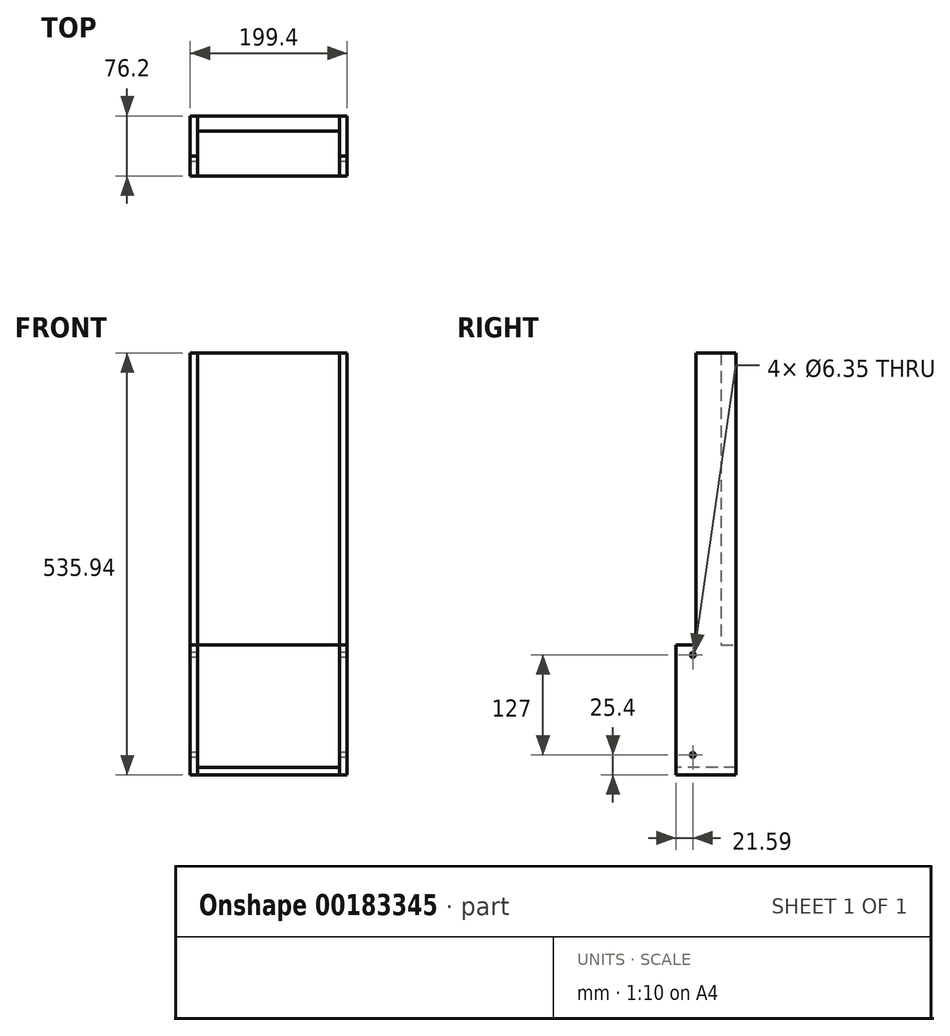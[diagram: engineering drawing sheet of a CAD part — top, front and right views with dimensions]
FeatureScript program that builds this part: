
annotation { "Feature Type Name" : "Feature", "Feature Type Description" : "" }
export const myFeature = defineFeature(function(context is Context, id is Id, definition is map)
    precondition{}
    {
        {
            var Q0;
            Q0=qCreatedBy(makeId("Front.planeOp"),FACE);
            var sketch = newSketch(context, id + "F0", { "sketchPlane" : qUnion([Q0])});
            skLineSegment(sketch, "E0.bottom", {"start": v(90.17, 185.42) * mm, "end": v(-90.17, 185.42) * mm});
            skLineSegment(sketch, "E0.top", {"start": v(90.17, -185.42) * mm, "end": v(-90.17, -185.42) * mm});
            skLineSegment(sketch, "E0.left", {"start": v(90.17, 185.42) * mm, "end": v(90.17, -185.42) * mm});
            skLineSegment(sketch, "E0.right", {"start": v(-90.17, 185.42) * mm, "end": v(-90.17, -185.42) * mm});
            skPoint(sketch, "E0.middle", {"position": v(0, 0) * mm});
            skSolve(sketch);
        }
        {
            var Q0;
            Q0 = qSketchRegion(id + "F0", true);
            extrude(context, id + "F1", {"entities" : qUnion([Q0]), "depth" : 19.05 * mm});
        }
        {
            var Q0;
            Q0=qCreatedBy(makeId("Right.planeOp"),FACE);
            var sketch = newSketch(context, id + "F2", { "sketchPlane" : qUnion([Q0])});
            skLineSegment(sketch, "E1", {"start": v(0, 0) * mm, "end": v(-162.56, 0) * mm, "construction": true});
            skLineSegment(sketch, "E2", {"start": v(-162.56, 0) * mm, "end": v(-162.56, -490.22) * mm, "construction": true});
            skLineSegment(sketch, "E3", {"start": v(0, 0) * mm, "end": v(0, -490.22) * mm, "construction": true});
            skLineSegment(sketch, "E4", {"start": v(468.47, -490.22) * mm, "end": v(-664.71, -490.22) * mm, "construction": true});
            skLineSegment(sketch, "E5", {"start": v(0, -325.12) * mm, "end": v(-162.56, -325.12) * mm, "construction": true});
            skLineSegment(sketch, "E6", {"start": v(-54.6, -325.12) * mm, "end": v(-54.6, -198.12) * mm, "construction": true});
            skLineSegment(sketch, "E7", {"start": v(-54.6, -198.12) * mm, "end": v(-162.56, -198.12) * mm, "construction": true});
            skSolve(sketch);
        }
        {
            var Q0;
            Q0=makeQuery(id+"F1.opExtrude","SWEPT_FACE",FACE,{"disambiguationData":[OSD([sQuery(id+"F0.wireOp",EDGE,"E0.right")])]});
            var sketch = newSketch(context, id + "F3", { "sketchPlane" : qUnion([Q0])});
            skLineSegment(sketch, "E8.bottom", {"start": v(0, 185.42) * mm, "end": v(50.8, 185.42) * mm});
            skLineSegment(sketch, "E8.top", {"start": v(0, -350.52) * mm, "end": v(50.8, -350.52) * mm});
            skLineSegment(sketch, "E8.left", {"start": v(0, 185.42) * mm, "end": v(0, -350.52) * mm});
            skLineSegment(sketch, "E8.right", {"start": v(50.8, 185.42) * mm, "end": v(50.8, -185.42) * mm});
            skLineSegment(sketch, "E9", {"start": v(50.8, -185.42) * mm, "end": v(76.2, -185.42) * mm});
            skLineSegment(sketch, "E10", {"start": v(76.2, -185.42) * mm, "end": v(76.2, -350.52) * mm});
            skLineSegment(sketch, "E11", {"start": v(76.2, -350.52) * mm, "end": v(50.8, -350.52) * mm});
            skSolve(sketch);
        }
        {
            var Q0;
            Q0 = qSketchRegion(id + "F3", true);
            extrude(context, id + "F4", {"entities" : qUnion([Q0]), "depth" : 9.52 * mm});
        }
        {
            var Q0;
            Q0=makeQuery(id+"F4.opExtrude","SWEPT_BODY",BODY,{"disambiguationData":[OSD([sQuery(id+"F3.wireOp",EDGE,"E8.bottom"),sQuery(id+"F3.wireOp",EDGE,"E8.top"),sQuery(id+"F3.wireOp",EDGE,"E8.left"),sQuery(id+"F3.wireOp",EDGE,"E8.right")])]});
            var Q1;
            Q1=qCreatedBy(makeId("Right.planeOp"),FACE);
            mirror(context, id + "F5", {"entities" : qUnion([Q0]), "mirrorPlane" : qUnion([Q1])});
        }
        {
            var Q0;
            Q0=makeQuery(id+"F5.opPattern","COPY",FACE,{"derivedFrom":makeQuery(id+"F4.opExtrude","CAP_FACE",FACE,{"disambiguationData":[OSD([sQuery(id+"F3.wireOp",EDGE,"E8.bottom"),sQuery(id+"F3.wireOp",EDGE,"E8.top"),sQuery(id+"F3.wireOp",EDGE,"E8.left"),sQuery(id+"F3.wireOp",EDGE,"E8.right"),sQuery(id+"F3.wireOp",EDGE,"E9"),sQuery(id+"F3.wireOp",EDGE,"E10"),sQuery(id+"F3.wireOp",EDGE,"E11")])],"isStart":true}),"instanceName":"1"});
            var sketch = newSketch(context, id + "F6", { "sketchPlane" : qUnion([Q0])});
            skLineSegment(sketch, "E12.bottom", {"start": v(0, -350.52) * mm, "end": v(76.2, -350.52) * mm});
            skLineSegment(sketch, "E12.top", {"start": v(0, -341) * mm, "end": v(76.2, -341) * mm});
            skLineSegment(sketch, "E12.left", {"start": v(0, -350.52) * mm, "end": v(0, -341) * mm});
            skLineSegment(sketch, "E12.right", {"start": v(76.2, -350.52) * mm, "end": v(76.2, -341) * mm});
            skSolve(sketch);
        }
        {
            var Q0;
            Q0=makeQuery(id+"F6.imprint","IMPRINT",FACE,{"disambiguationData":[TD([[makeQuery(id+"F6.imprint","IMPRINT",EDGE,{"derivedFrom":sQuery(id+"F6.wireOp",EDGE,"E12.bottom")}),1.0]])]});
            var Q1;
            Q1=makeQuery(id+"F4.opExtrude","CAP_FACE",FACE,{"disambiguationData":[OSD([sQuery(id+"F3.wireOp",EDGE,"E8.bottom"),sQuery(id+"F3.wireOp",EDGE,"E8.top"),sQuery(id+"F3.wireOp",EDGE,"E8.left"),sQuery(id+"F3.wireOp",EDGE,"E8.right"),sQuery(id+"F3.wireOp",EDGE,"E9"),sQuery(id+"F3.wireOp",EDGE,"E10"),sQuery(id+"F3.wireOp",EDGE,"E11")])],"isStart":true});
            extrude(context, id + "F7", {"entities" : qUnion([Q0]), "endBound" : BoundingType.UP_TO_SURFACE, "endBoundEntityFace" : qUnion([Q1]), "depth" : 25.4 * mm});
        }
        {
            var Q0;
            Q0=makeQuery(id+"F4.opExtrude","CAP_FACE",FACE,{"disambiguationData":[OSD([sQuery(id+"F3.wireOp",EDGE,"E8.bottom"),sQuery(id+"F3.wireOp",EDGE,"E8.top"),sQuery(id+"F3.wireOp",EDGE,"E8.left"),sQuery(id+"F3.wireOp",EDGE,"E8.right"),sQuery(id+"F3.wireOp",EDGE,"E9"),sQuery(id+"F3.wireOp",EDGE,"E10"),sQuery(id+"F3.wireOp",EDGE,"E11")])],"isStart":false});
            var sketch = newSketch(context, id + "F8", { "sketchPlane" : qUnion([Q0])});
            skCircle(sketch, "E13", {"center": v(54.6, -198.12) * mm, "radius": 3.18 * mm});
            skCircle(sketch, "E14", {"center": v(54.6, -325.12) * mm, "radius": 3.18 * mm});
            skSolve(sketch);
        }
        {
            var Q0;
            Q0 = qSketchRegion(id + "F8", true);
            extrude(context, id + "F9", {"entities" : qUnion([Q0]), "operationType" : NewBodyOperationType.REMOVE, "endBound" : BoundingType.THROUGH_ALL, "oppositeDirection" : true, "depth" : 25.4 * mm});
        }
    });
